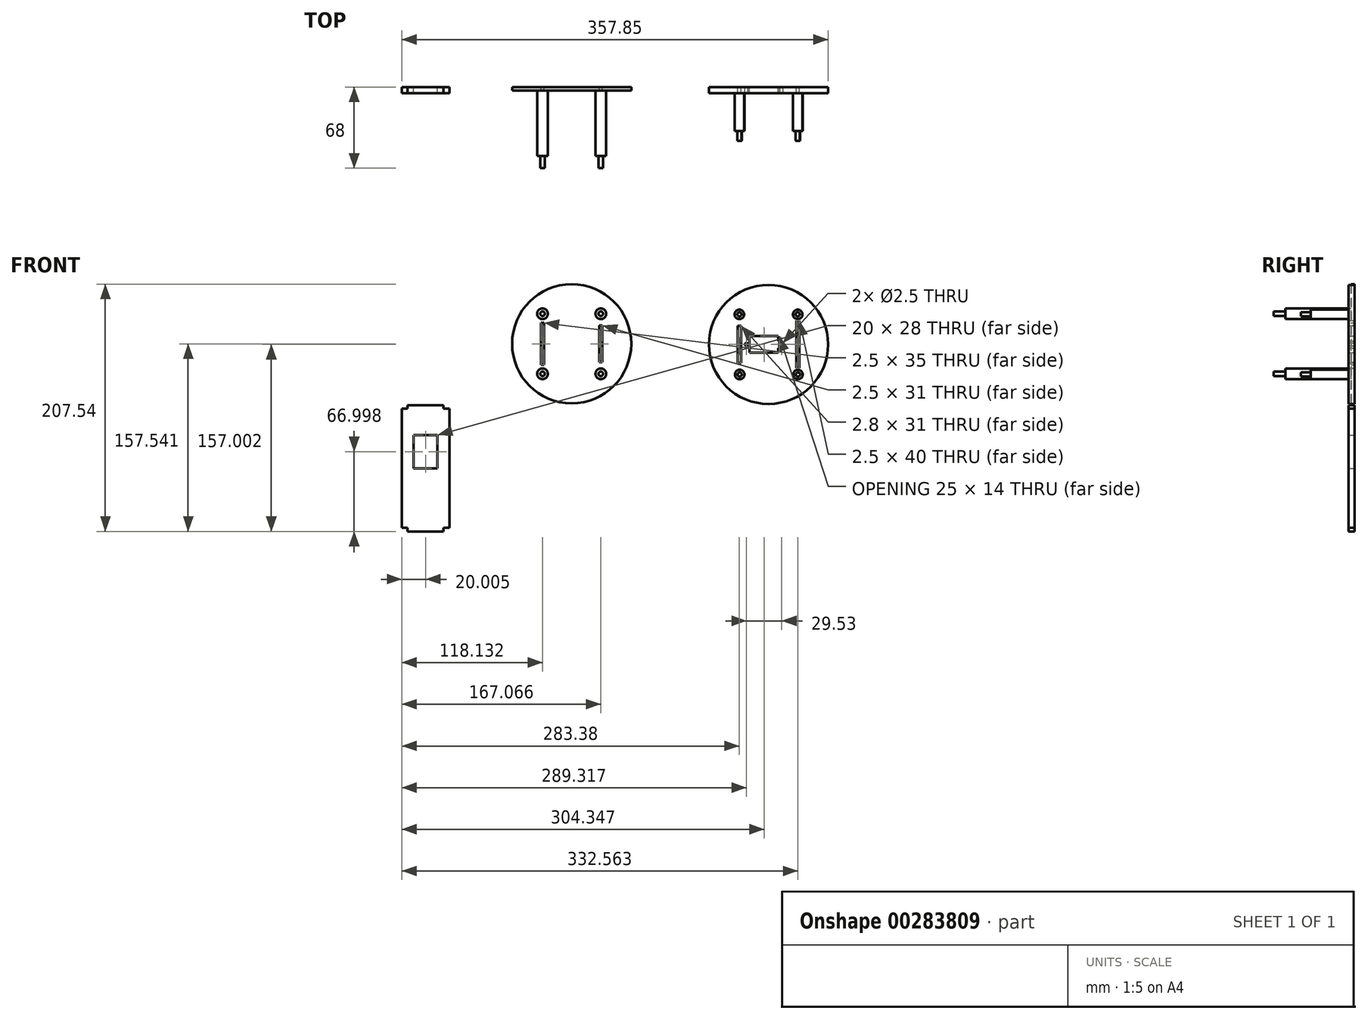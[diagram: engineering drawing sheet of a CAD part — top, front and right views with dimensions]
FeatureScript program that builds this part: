
annotation { "Feature Type Name" : "Feature", "Feature Type Description" : "" }
export const myFeature = defineFeature(function(context is Context, id is Id, definition is map)
    precondition{}
    {
        {
            var Q0;
            Q0=qCreatedBy(makeId("Front.planeOp"),FACE);
            var sketch = newSketch(context, id + "F0", { "sketchPlane" : qUnion([Q0])});
            skCircle(sketch, "E0", {"center": v(-135.34, 127.87) * mm, "radius": 50 * mm});
            skLineSegment(sketch, "E1.bottom", {"start": v(-271.12, 161.63) * mm, "end": v(-330.06, 161.63) * mm});
            skLineSegment(sketch, "E1.top", {"start": v(-271.12, 95.19) * mm, "end": v(-330.06, 95.19) * mm});
            skLineSegment(sketch, "E1.left", {"start": v(-266.12, 156.63) * mm, "end": v(-266.12, 100.19) * mm});
            skLineSegment(sketch, "E1.right", {"start": v(-335.06, 156.63) * mm, "end": v(-335.06, 100.19) * mm});
            skPoint(sketch, "E2", {"position": v(-300.6, 161.63) * mm});
            skPoint(sketch, "E3", {"position": v(-266.12, 128.41) * mm});
            skPoint(sketch, "E4", {"position": v(-335.06, 128.41) * mm});
            skPoint(sketch, "E5", {"position": v(-300.6, 95.19) * mm});
            skCircle(sketch, "E6", {"center": v(-325.06, 153.63) * mm, "radius": 4.5 * mm});
            skCircle(sketch, "E7", {"center": v(-276.12, 153.63) * mm, "radius": 4.5 * mm});
            skCircle(sketch, "E8", {"center": v(-276.12, 103.19) * mm, "radius": 4.5 * mm});
            skCircle(sketch, "E9", {"center": v(-325.06, 103.19) * mm, "radius": 4.5 * mm});
            skPoint(sketch, "E10.visualSharp", {"position": v(-335.06, 161.63) * mm});
            skArc(sketch, "E10.filletArc", {"start": v(-330.06, 161.63) * mm, "mid": v(-333.6, 160.17) * mm, "end": v(-335.06, 156.63) * mm});
            skPoint(sketch, "E11.visualSharp", {"position": v(-266.12, 161.63) * mm});
            skArc(sketch, "E11.filletArc", {"start": v(-266.12, 156.63) * mm, "mid": v(-267.59, 160.17) * mm, "end": v(-271.12, 161.63) * mm});
            skPoint(sketch, "E12.visualSharp", {"position": v(-266.12, 95.19) * mm});
            skArc(sketch, "E12.filletArc", {"start": v(-271.12, 95.19) * mm, "mid": v(-267.59, 96.65) * mm, "end": v(-266.12, 100.19) * mm});
            skPoint(sketch, "E13.visualSharp", {"position": v(-335.06, 95.19) * mm});
            skArc(sketch, "E13.filletArc", {"start": v(-335.06, 100.19) * mm, "mid": v(-333.6, 96.65) * mm, "end": v(-330.06, 95.19) * mm});
            skLineSegment(sketch, "E14.bottom", {"start": v(-277.37, 143.91) * mm, "end": v(-274.87, 143.91) * mm});
            skLineSegment(sketch, "E14.top", {"start": v(-277.37, 112.91) * mm, "end": v(-274.87, 112.91) * mm});
            skLineSegment(sketch, "E14.left", {"start": v(-277.37, 143.91) * mm, "end": v(-277.37, 112.91) * mm});
            skLineSegment(sketch, "E14.right", {"start": v(-274.87, 143.91) * mm, "end": v(-274.87, 112.91) * mm});
            skPoint(sketch, "E14.middle", {"position": v(-276.12, 128.41) * mm});
            skCircle(sketch, "E15", {"center": v(-325.06, 103.19) * mm, "radius": 1.9 * mm});
            skCircle(sketch, "E16", {"center": v(-276.12, 103.19) * mm, "radius": 1.9 * mm});
            skCircle(sketch, "E17", {"center": v(-325.06, 153.63) * mm, "radius": 1.9 * mm});
            skCircle(sketch, "E18", {"center": v(-276.12, 153.63) * mm, "radius": 1.9 * mm});
            skLineSegment(sketch, "E19.bottom", {"start": v(-323.8, 110.91) * mm, "end": v(-326.3, 110.91) * mm});
            skLineSegment(sketch, "E19.top", {"start": v(-323.8, 145.91) * mm, "end": v(-326.3, 145.91) * mm});
            skLineSegment(sketch, "E19.left", {"start": v(-323.8, 110.91) * mm, "end": v(-323.8, 145.91) * mm});
            skLineSegment(sketch, "E19.right", {"start": v(-326.3, 110.91) * mm, "end": v(-326.3, 145.91) * mm});
            skPoint(sketch, "E19.middle", {"position": v(-325.06, 128.41) * mm});
            skLineSegment(sketch, "E20.bottom", {"start": v(-127.34, 134.87) * mm, "end": v(-151.34, 134.87) * mm});
            skLineSegment(sketch, "E20.top", {"start": v(-127.34, 120.87) * mm, "end": v(-151.34, 120.87) * mm});
            skLineSegment(sketch, "E20.left", {"start": v(-127.34, 134.87) * mm, "end": v(-127.34, 120.87) * mm});
            skLineSegment(sketch, "E20.right", {"start": v(-151.34, 134.87) * mm, "end": v(-151.34, 120.87) * mm});
            skLineSegment(sketch, "E21.bottom", {"start": v(-126.34, 130.87) * mm, "end": v(-127.34, 130.87) * mm});
            skLineSegment(sketch, "E21.top", {"start": v(-126.34, 124.87) * mm, "end": v(-127.34, 124.87) * mm});
            skLineSegment(sketch, "E21.left", {"start": v(-126.34, 130.87) * mm, "end": v(-126.34, 124.87) * mm});
            skLineSegment(sketch, "E21.right", {"start": v(-127.34, 130.87) * mm, "end": v(-127.34, 124.87) * mm});
            skCircle(sketch, "E22", {"center": v(-124.34, 127.87) * mm, "radius": 1.25 * mm});
            skCircle(sketch, "E23", {"center": v(-153.87, 127.87) * mm, "radius": 1.25 * mm});
            skPoint(sketch, "E24", {"position": v(-151.34, 127.87) * mm});
            skPoint(sketch, "E25", {"position": v(-126.34, 127.87) * mm});
            skPoint(sketch, "E26", {"position": v(-127.34, 127.87) * mm});
            skLineSegment(sketch, "E27", {"start": v(-132.9, 127.87) * mm, "end": v(-253.96, 127.87) * mm, "construction": true});
            skPoint(sketch, "E28", {"position": v(-135.34, 134.87) * mm});
            skCircle(sketch, "E29", {"center": v(-159.81, 153.1) * mm, "radius": 4 * mm});
            skCircle(sketch, "E30", {"center": v(-110.88, 153.1) * mm, "radius": 4 * mm});
            skCircle(sketch, "E31", {"center": v(-110.63, 102.65) * mm, "radius": 4 * mm});
            skCircle(sketch, "E32", {"center": v(-159.56, 102.65) * mm, "radius": 4 * mm});
            skPoint(sketch, "E33.visualSharp", {"position": v(-169.56, 161.1) * mm});
            skPoint(sketch, "E34.visualSharp", {"position": v(-100.63, 161.1) * mm});
            skPoint(sketch, "E35.visualSharp", {"position": v(-100.63, 94.65) * mm});
            skPoint(sketch, "E36.visualSharp", {"position": v(-169.56, 94.65) * mm});
            skLineSegment(sketch, "E37.bottom", {"start": v(-161.21, 143.37) * mm, "end": v(-158.41, 143.37) * mm});
            skLineSegment(sketch, "E37.top", {"start": v(-161.21, 112.37) * mm, "end": v(-158.41, 112.37) * mm});
            skLineSegment(sketch, "E37.left", {"start": v(-161.21, 143.37) * mm, "end": v(-161.21, 112.37) * mm});
            skLineSegment(sketch, "E37.right", {"start": v(-158.41, 143.37) * mm, "end": v(-158.41, 112.37) * mm});
            skLineSegment(sketch, "E38.bottom", {"start": v(-109.38, 107.87) * mm, "end": v(-111.88, 107.87) * mm});
            skLineSegment(sketch, "E38.top", {"start": v(-109.38, 147.87) * mm, "end": v(-111.88, 147.87) * mm});
            skLineSegment(sketch, "E38.left", {"start": v(-109.38, 107.87) * mm, "end": v(-109.38, 147.87) * mm});
            skLineSegment(sketch, "E38.right", {"start": v(-111.88, 107.87) * mm, "end": v(-111.88, 147.87) * mm});
            skLineSegment(sketch, "E39.bottom", {"start": v(-403.19, -26.13) * mm, "end": v(-408.37, -26.13) * mm});
            skLineSegment(sketch, "E39.top", {"start": v(-403.19, 73.87) * mm, "end": v(-408.37, 73.87) * mm});
            skLineSegment(sketch, "E39.left", {"start": v(-403.19, -26.13) * mm, "end": v(-403.19, 73.87) * mm});
            skLineSegment(sketch, "E39.right", {"start": v(-443.19, -26.13) * mm, "end": v(-443.19, 73.87) * mm});
            skPoint(sketch, "E39.middle", {"position": v(-423.19, 23.87) * mm});
            skLineSegment(sketch, "E40.bottom", {"start": v(-408.37, -29.13) * mm, "end": v(-438.37, -29.13) * mm});
            skLineSegment(sketch, "E40.left", {"start": v(-408.37, -29.13) * mm, "end": v(-408.37, -26.13) * mm});
            skLineSegment(sketch, "E40.right", {"start": v(-438.37, -29.13) * mm, "end": v(-438.37, -26.13) * mm});
            skLineSegment(sketch, "E41.bottom", {"start": v(-408.37, 76.87) * mm, "end": v(-438.37, 76.87) * mm});
            skLineSegment(sketch, "E41.left", {"start": v(-408.37, 76.87) * mm, "end": v(-408.37, 73.87) * mm});
            skLineSegment(sketch, "E41.right", {"start": v(-438.37, 76.87) * mm, "end": v(-438.37, 73.87) * mm});
            skLineSegment(sketch, "E42.trimOffspring", {"start": v(-438.37, 73.87) * mm, "end": v(-443.19, 73.87) * mm});
            skLineSegment(sketch, "E43.trimOffspring", {"start": v(-438.37, -26.13) * mm, "end": v(-443.19, -26.13) * mm});
            skLineSegment(sketch, "E44.bottom", {"start": v(-413.19, 23.87) * mm, "end": v(-433.19, 23.87) * mm});
            skLineSegment(sketch, "E44.top", {"start": v(-413.19, 51.87) * mm, "end": v(-433.19, 51.87) * mm});
            skLineSegment(sketch, "E44.left", {"start": v(-413.19, 23.87) * mm, "end": v(-413.19, 51.87) * mm});
            skLineSegment(sketch, "E44.right", {"start": v(-433.19, 23.87) * mm, "end": v(-433.19, 51.87) * mm});
            skPoint(sketch, "E44.middle", {"position": v(-423.19, 37.87) * mm});
            skCircle(sketch, "E45", {"center": v(-159.81, 153.1) * mm, "radius": 1.75 * mm});
            skCircle(sketch, "E46", {"center": v(-110.88, 153.1) * mm, "radius": 1.75 * mm});
            skCircle(sketch, "E47", {"center": v(-110.63, 102.65) * mm, "radius": 1.75 * mm});
            skCircle(sketch, "E48", {"center": v(-159.56, 102.65) * mm, "radius": 1.75 * mm});
            skPoint(sketch, "E49", {"position": v(-110.63, 107.87) * mm});
            skPoint(sketch, "E50", {"position": v(-300.6, 128.41) * mm});
            skCircle(sketch, "E51", {"center": v(-300.6, 128.41) * mm, "radius": 50 * mm});
            skLineSegment(sketch, "E52.bottom", {"start": v(-304.06, -5.01) * mm, "end": v(-304.06, 0.17) * mm});
            skLineSegment(sketch, "E52.top", {"start": v(-204.06, -5.01) * mm, "end": v(-204.06, 0.17) * mm});
            skLineSegment(sketch, "E52.left", {"start": v(-304.06, -5.01) * mm, "end": v(-204.06, -5.01) * mm});
            skLineSegment(sketch, "E52.right", {"start": v(-304.06, 34.99) * mm, "end": v(-204.06, 34.99) * mm});
            skLineSegment(sketch, "E53.bottom", {"start": v(-307.06, 0.17) * mm, "end": v(-307.06, 30.17) * mm});
            skLineSegment(sketch, "E53.left", {"start": v(-307.06, 0.17) * mm, "end": v(-304.06, 0.17) * mm});
            skLineSegment(sketch, "E53.right", {"start": v(-307.06, 30.17) * mm, "end": v(-304.06, 30.17) * mm});
            skLineSegment(sketch, "E54.bottom", {"start": v(-201.06, 0.17) * mm, "end": v(-201.06, 30.17) * mm});
            skLineSegment(sketch, "E54.left", {"start": v(-201.06, 0.17) * mm, "end": v(-204.06, 0.17) * mm});
            skLineSegment(sketch, "E54.right", {"start": v(-201.06, 30.17) * mm, "end": v(-204.06, 30.17) * mm});
            skLineSegment(sketch, "E55.trimOffspring", {"start": v(-204.06, 30.17) * mm, "end": v(-204.06, 34.99) * mm});
            skLineSegment(sketch, "E56.trimOffspring", {"start": v(-304.06, 30.17) * mm, "end": v(-304.06, 34.99) * mm});
            skPoint(sketch, "E57", {"position": v(-307.06, 15.17) * mm});
            skPoint(sketch, "E58", {"position": v(-201.06, 15.17) * mm});
            skPoint(sketch, "E59", {"position": v(-254.06, 34.99) * mm});
            skPoint(sketch, "E60", {"position": v(-254.06, -5.01) * mm});
            skLineSegment(sketch, "E61.bottom", {"start": v(-282.96, 27.8) * mm, "end": v(-204.96, 27.8) * mm});
            skLineSegment(sketch, "E61.top", {"start": v(-282.96, 25.8) * mm, "end": v(-204.96, 25.8) * mm});
            skLineSegment(sketch, "E61.left", {"start": v(-282.96, 27.8) * mm, "end": v(-282.96, 25.8) * mm});
            skLineSegment(sketch, "E61.right", {"start": v(-204.96, 27.8) * mm, "end": v(-204.96, 25.8) * mm});
            skLineSegment(sketch, "E62.bottom", {"start": v(-282.96, 4.55) * mm, "end": v(-204.96, 4.55) * mm});
            skLineSegment(sketch, "E62.top", {"start": v(-282.96, 2.55) * mm, "end": v(-204.96, 2.55) * mm});
            skLineSegment(sketch, "E62.left", {"start": v(-282.96, 4.55) * mm, "end": v(-282.96, 2.55) * mm});
            skLineSegment(sketch, "E62.right", {"start": v(-204.96, 4.55) * mm, "end": v(-204.96, 2.55) * mm});
            skLineSegment(sketch, "E63", {"start": v(-239.63, 25.8) * mm, "end": v(-239.63, 4.55) * mm, "construction": true});
            skPoint(sketch, "E64", {"position": v(-239.63, 15.17) * mm});
            skPoint(sketch, "E65", {"position": v(-254.06, 15.17) * mm});
            skSolve(sketch);
        }
        {
            var Q0;
            Q0=makeQuery(id+"F0.imprint","IMPRINT",FACE,{"disambiguationData":[TD([[makeQuery(id+"F0.imprint","IMPRINT",EDGE,{"derivedFrom":sQuery(id+"F0.wireOp",EDGE,"E0")}),1.0]])]});
            extrude(context, id + "F1", {"entities" : qUnion([Q0]), "depth" : 5 * mm, "offsetDistance" : 25 * mm});
        }
        {
            var Q0;
            Q0=makeQuery(id+"F0.imprint","IMPRINT",FACE,{"disambiguationData":[TD([[makeQuery(id+"F0.imprint","IMPRINT",EDGE,{"derivedFrom":sQuery(id+"F0.wireOp",EDGE,"E32")}),1.0]])]});
            var Q1;
            Q1=makeQuery(id+"F0.imprint","IMPRINT",FACE,{"disambiguationData":[TD([[makeQuery(id+"F0.imprint","IMPRINT",EDGE,{"derivedFrom":sQuery(id+"F0.wireOp",EDGE,"E31")}),1.0]])]});
            var Q2;
            Q2=makeQuery(id+"F0.imprint","IMPRINT",FACE,{"disambiguationData":[TD([[makeQuery(id+"F0.imprint","IMPRINT",EDGE,{"derivedFrom":sQuery(id+"F0.wireOp",EDGE,"E30")}),1.0]])]});
            var Q3;
            Q3=makeQuery(id+"F0.imprint","IMPRINT",FACE,{"disambiguationData":[TD([[makeQuery(id+"F0.imprint","IMPRINT",EDGE,{"derivedFrom":sQuery(id+"F0.wireOp",EDGE,"E29")}),1.0]])]});
            extrude(context, id + "F2", {"entities" : qUnion([Q0, Q1, Q2, Q3]), "operationType" : NewBodyOperationType.ADD, "depth" : 37 * mm, "offsetDistance" : 25 * mm});
        }
        {
            var Q0;
            Q0=makeQuery(id+"F0.imprint","IMPRINT",FACE,{"disambiguationData":[TD([[makeQuery(id+"F0.imprint","IMPRINT",EDGE,{"derivedFrom":sQuery(id+"F0.wireOp",EDGE,"E45")}),1.0]])]});
            var Q1;
            Q1=makeQuery(id+"F0.imprint","IMPRINT",FACE,{"disambiguationData":[TD([[makeQuery(id+"F0.imprint","IMPRINT",EDGE,{"derivedFrom":sQuery(id+"F0.wireOp",EDGE,"E46")}),1.0]])]});
            var Q2;
            Q2=makeQuery(id+"F0.imprint","IMPRINT",FACE,{"disambiguationData":[TD([[makeQuery(id+"F0.imprint","IMPRINT",EDGE,{"derivedFrom":sQuery(id+"F0.wireOp",EDGE,"E47")}),1.0]])]});
            var Q3;
            Q3=makeQuery(id+"F0.imprint","IMPRINT",FACE,{"disambiguationData":[TD([[makeQuery(id+"F0.imprint","IMPRINT",EDGE,{"derivedFrom":sQuery(id+"F0.wireOp",EDGE,"E48")}),1.0]])]});
            extrude(context, id + "F3", {"entities" : qUnion([Q0, Q1, Q2, Q3]), "operationType" : NewBodyOperationType.ADD, "depth" : 45 * mm, "offsetDistance" : 25 * mm});
        }
        {
            var Q0;
            Q0=makeQuery(id+"F0.imprint","IMPRINT",FACE,{"disambiguationData":[TD([[makeQuery(id+"F0.imprint","IMPRINT",EDGE,{"derivedFrom":sQuery(id+"F0.wireOp",EDGE,"E39.bottom")}),-1.0]])]});
            extrude(context, id + "F4", {"entities" : qUnion([Q0]), "depth" : 5 * mm, "offsetDistance" : 25 * mm});
        }
        {
            var Q0;
            Q0=makeQuery(id+"F0.imprint","IMPRINT",FACE,{"disambiguationData":[TD([[makeQuery(id+"F0.imprint","IMPRINT",EDGE,{"derivedFrom":sQuery(id+"F0.wireOp",EDGE,"E1.bottom")}),-1.0]])]});
            var Q1;
            Q1=makeQuery(id+"F0.imprint","IMPRINT",FACE,{"disambiguationData":[TD([[makeQuery(id+"F0.imprint","IMPRINT",EDGE,{"derivedFrom":sQuery(id+"F0.wireOp",EDGE,"E1.bottom")}),1.0]])]});
            extrude(context, id + "F5", {"entities" : qUnion([Q0, Q1]), "depth" : 3 * mm, "offsetDistance" : 25 * mm});
        }
        {
            var Q0;
            Q0=makeQuery(id+"F0.imprint","IMPRINT",FACE,{"disambiguationData":[TD([[makeQuery(id+"F0.imprint","IMPRINT",EDGE,{"derivedFrom":sQuery(id+"F0.wireOp",EDGE,"E6")}),1.0]])]});
            var Q1;
            Q1=makeQuery(id+"F0.imprint","IMPRINT",FACE,{"disambiguationData":[TD([[makeQuery(id+"F0.imprint","IMPRINT",EDGE,{"derivedFrom":sQuery(id+"F0.wireOp",EDGE,"E7")}),1.0]])]});
            var Q2;
            Q2=makeQuery(id+"F0.imprint","IMPRINT",FACE,{"disambiguationData":[TD([[makeQuery(id+"F0.imprint","IMPRINT",EDGE,{"derivedFrom":sQuery(id+"F0.wireOp",EDGE,"E8")}),1.0]])]});
            var Q3;
            Q3=makeQuery(id+"F0.imprint","IMPRINT",FACE,{"disambiguationData":[TD([[makeQuery(id+"F0.imprint","IMPRINT",EDGE,{"derivedFrom":sQuery(id+"F0.wireOp",EDGE,"E9")}),1.0]])]});
            extrude(context, id + "F6", {"entities" : qUnion([Q0, Q1, Q2, Q3]), "operationType" : NewBodyOperationType.ADD, "depth" : 58 * mm, "offsetDistance" : 25 * mm});
        }
        {
            var Q0;
            Q0=makeQuery(id+"F0.imprint","IMPRINT",FACE,{"disambiguationData":[TD([[makeQuery(id+"F0.imprint","IMPRINT",EDGE,{"derivedFrom":sQuery(id+"F0.wireOp",EDGE,"E17")}),1.0]])]});
            var Q1;
            Q1=makeQuery(id+"F0.imprint","IMPRINT",FACE,{"disambiguationData":[TD([[makeQuery(id+"F0.imprint","IMPRINT",EDGE,{"derivedFrom":sQuery(id+"F0.wireOp",EDGE,"E18")}),1.0]])]});
            var Q2;
            Q2=makeQuery(id+"F0.imprint","IMPRINT",FACE,{"disambiguationData":[TD([[makeQuery(id+"F0.imprint","IMPRINT",EDGE,{"derivedFrom":sQuery(id+"F0.wireOp",EDGE,"E16")}),1.0]])]});
            var Q3;
            Q3=makeQuery(id+"F0.imprint","IMPRINT",FACE,{"disambiguationData":[TD([[makeQuery(id+"F0.imprint","IMPRINT",EDGE,{"derivedFrom":sQuery(id+"F0.wireOp",EDGE,"E15")}),1.0]])]});
            extrude(context, id + "F7", {"entities" : qUnion([Q0, Q1, Q2, Q3]), "operationType" : NewBodyOperationType.ADD, "depth" : 68 * mm, "offsetDistance" : 25 * mm});
        }
    });
